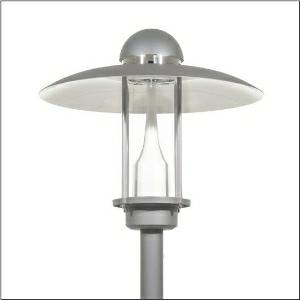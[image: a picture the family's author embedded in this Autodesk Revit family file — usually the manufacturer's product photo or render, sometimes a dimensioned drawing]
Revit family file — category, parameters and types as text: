
# Revit family: city-light_elegance_iq___st1_2a_5xa5265af14h_1cc4
name_source: partatom
category: Lighting Fixtures
units: mm (PartAtom-declared; Revit-internal decimal feet)

## family parameters
Cut with Voids When Loaded = No
Host = Face
Light Source = No
Part Type = Normal
Room Calculation Point = No
Round Connector Dimension = Use Diameter
Shared = No

## types (1)
- --- (1 x LED, 1470 lm, 12.9 W, 2200K)
    Apparent Load = 13 VA
    CIE Flux Codes = 22 62 94 98 100
    Color Rendering = 70
    Color Temperature = 2200K
    Default Elevation = 1800 mm
    Description = City-Light Elegance iQ, mast luminaire, Module 540 iQ-SR, primary light control with 3 zone facetted reflector, of plastic, silver coated, highly specular, structured, primary optical cover: cover, of PMMA, transparent, light distribution: ST1.2a, light emission: direct distribution, primary light characteristic: asymmetric, installation type: post-top, LED, High Power LED, rated luminous flux: 1.470lm, luminous efficacy: 114lm/W, light colour: 722, colour temperature: 2200K, control gear: ECG iQ, control: presetting dimming logarithmic, Street-Remote, Auto-Match, Temp-Guard, Lumen-Switch, Night-Set, Smart-Wire, Light-Fading, Desk-Remote (wireless, voltage-free reading and setting of iQ features in the workshop via application-optimized NFC function/RFID function), optimised constant luminous flux control (CLO 2.0), with terminal, 6-pole, max. 2.5mm², mains connection: 220..240V, AC, 50/60Hz, start of lifetime: 13W, end of lifetime: 13W, reduction: 6W, luminaire housing, upper part, of aluminium, coated, Siteco® metallic grey (DB 702S), diameter: 750mm, height: 675mm, spigot size: d x l = 76 x 70mm (post-top) | with reducer (optional accessory) 60 x 70mm, post-top mast mounting element, of diecast aluminium, coated, Siteco® metallic grey (DB 702S), Module 540 iQ-SR, traffic white (RAL 9016), equipment: standard, protection rating (complete): IP65, insulation class (complete): insulation class II (safety insulation), certification: CE, ENEC, VDE, packaging unit: 1 piece

Light Distribution: ST1.2a
    Height = 675 mm
    Lamp = 1 x LED
    Lamp Light Flux = 1470 lm
    Lamp Power = 12.9 W
    Lamp count = 1
    Length = 750 mm
    Luminous efficacy = 114 lm/W
    Manufacturer = Siteco
    ModVariant = No
    Model = 5XA5265AF14H
    Number of Poles = 1
    OnlyDefault = Yes
    Power Factor = 1
    Product Name = City-Light Elegance iQ | ST1.2a
    Product group = mast luminaire | pylon top
    ProductGroupID = 6100
    Protection Class = Protection class II
    Protection Degree = IP 65
    RLX_Detail_Level = 1
    RlxData = <blob elided: 100545 chars, md5=9bd76650>
    Socket = socket
    Standby Power = 0 W
    System Light Flux = 1470 lm
    System Power = 13 W
    Type Comments = factory setting: luminous flux: 100 % | dim-lin: 254 | 516 mA
    Type Image = l_1006912.jpg
    URL = http://relux.com
    VarID = @adj_071133
    Voltage = 0 V
    Weight = 0.00 kg
    Width = 0 mm  [stored 0 ft]

note: [stored X ft] marks values corroborated as IEEE doubles in the binary element streams (Revit-internal decimal feet)

## geometry (parser evidence)
native form markers: Blend x4, Sweep x9
no freeform markers — native parametric forms only
